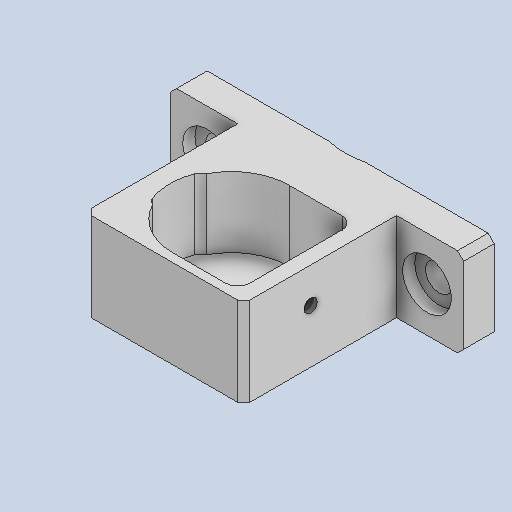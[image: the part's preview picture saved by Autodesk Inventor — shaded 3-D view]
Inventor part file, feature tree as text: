
AUTODESK INVENTOR PART (.ipt)
format: ipt  version: 2024.2 (Build 282272000, 272)  size: 233,472 bytes
history: native  units: in
note: dims shown in document units (in); Inventor stores cm internally (conversion verified against a paired STEP export)
features: extrude x5, hole x3, fillet x1, chamfer x1, sketch x1
ambient origin geometry x8: Origin, YZ Plane, XZ Plane, XY Plane, X Axis, Y Axis, Z Axis, Center Point
bodies: Solid1 (feature_tree)
feature tree (11):
  extrude  "Extrusion1"  Depth=0.0827in
  hole  "Hole1"  [1 undecoded]
  extrude  "Extrusion2"  TaperAngle=0.0deg  [1 undecoded]
  extrude  "Extrusion3"  TaperAngle=0.0deg  [1 undecoded]
  fillet  "Fillet1"  Radius=0.2362in
  hole  "Hole2"  [1 undecoded]
  chamfer  "Chamfer1"  Distance=1.0236in
  hole  "Hole3"  [1 undecoded]
  extrude  "Extrusion4"  Depth=0.5709in
  extrude  "Extrusion5"  Depth=0.0827in
  sketch  "Sketch5"  dims[d0=0.2854in d3=0.9449in d4=0.1969in d5=0.0in d6=0.1772in d7=0.328in d8=0.315in d9=0.0787in d10=0.5635in d11=0.4843in d12=0.0in d13=0.0in d14=0.0in d15=0.2362in d16=0.2362in d17=1.0236in d18=0.5118in d19=0.5709in d20=0.2854in d21=0.9843in d22=0.0in d23=0.0in d24=0.75in d26=0.0in d30=0.4173in d31=0.0in d32=0.376in d33=0.376in d35=0.0in d36=0.0787in d37=0.0849in d38=0.224in d39=0.315in d40=0.0787in d41=0.5635in d42=0.3492in d43=0.0in d46=0.75in d47=0.2264in d48=0.7913in d49=0.1201in d50=0.1201in d51=0.1374in d52=0.1374in d53=0.3356in d54=0.3356in d55=0.0394in d56=0.0787in d57=45.0deg d58=0.0394in d59=0.0413in d60=0.3937in d61=0.0in d62=0.0in d63=0.1969in d64=0.0827in d65=0.172in d66=0.1575in d67=0.0787in d68=90.0deg d69=0.0827in d70=0.0in d71=0.0827in d72=0.0in d73=0.0in d74=0.4862in d75=1.0in d76=0.0827in d77=0.0in]
note: 5 required parameter values undecoded (feature->parameter linkage not recoverable at this tier; creation-order binding heuristic only, values carry confidence <= 0.55)
